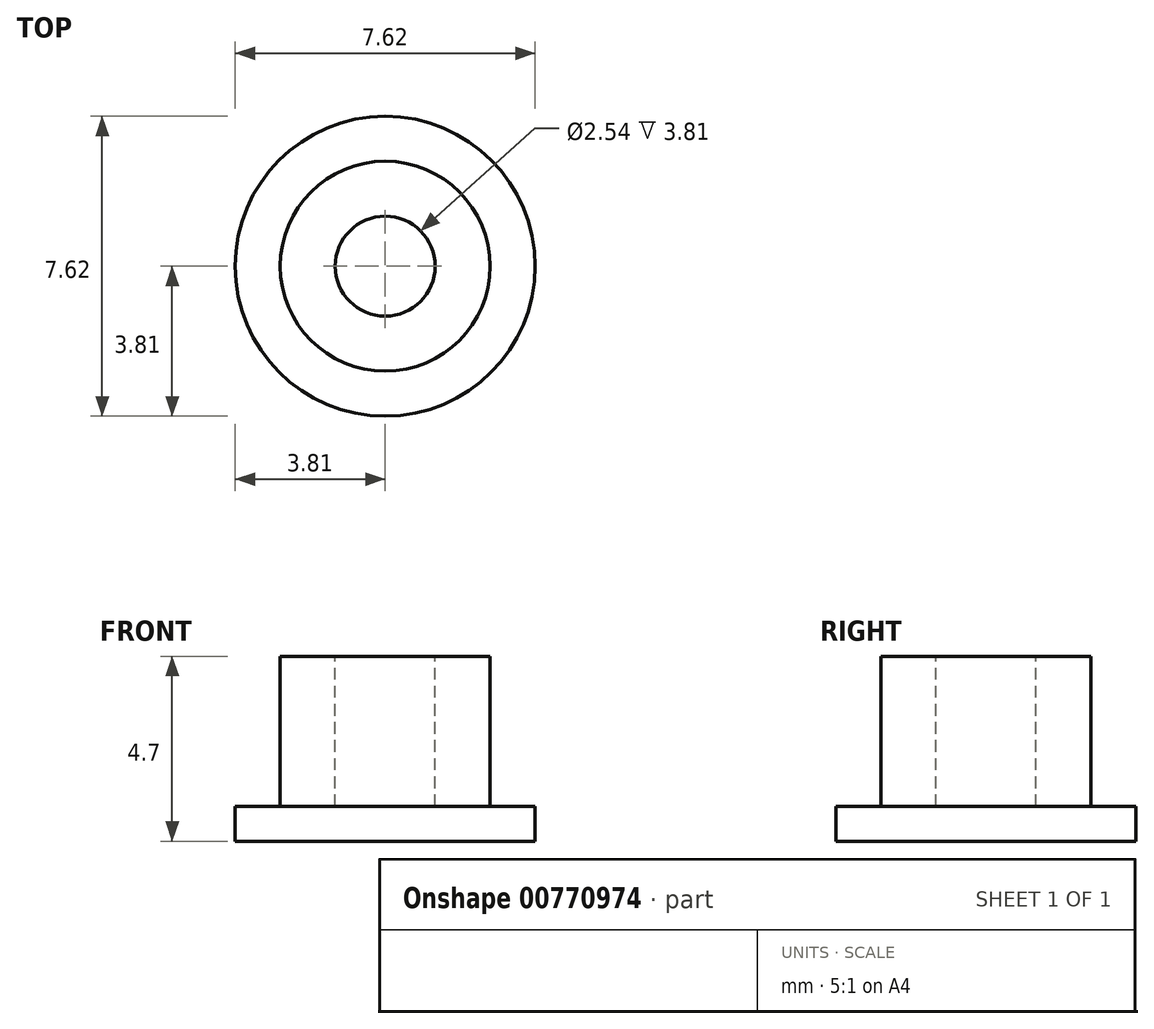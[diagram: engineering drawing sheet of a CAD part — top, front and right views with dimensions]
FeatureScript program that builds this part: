
annotation { "Feature Type Name" : "Feature", "Feature Type Description" : "" }
export const myFeature = defineFeature(function(context is Context, id is Id, definition is map)
    precondition{}
    {
        {
            var Q0;
            Q0=qCreatedBy(makeId("Top.planeOp"),FACE);
            var sketch = newSketch(context, id + "F0", { "sketchPlane" : qUnion([Q0])});
            skCircle(sketch, "E0", {"center": v(0, 0) * mm, "radius": 3.81 * mm});
            skSolve(sketch);
        }
        {
            var Q0;
            Q0=makeQuery(id+"F0.imprint","IMPRINT",FACE,{"disambiguationData":[TD([[makeQuery(id+"F0.imprint","IMPRINT",EDGE,{"derivedFrom":sQuery(id+"F0.wireOp",EDGE,"E0")}),1.0]])]});
            extrude(context, id + "F1", {"entities" : qUnion([Q0]), "depth" : 0.89 * mm, "offsetDistance" : 25.4 * mm});
        }
        {
            var Q0;
            Q0=makeQuery(id+"F1.opExtrude","CAP_FACE",FACE,{"disambiguationData":[OSD([sQuery(id+"F0.wireOp",EDGE,"E0")])],"isStart":false});
            var sketch = newSketch(context, id + "F2", { "sketchPlane" : qUnion([Q0])});
            skCircle(sketch, "E1", {"center": v(0, 0) * mm, "radius": 2.67 * mm});
            skSolve(sketch);
        }
        {
            var Q0;
            Q0=makeQuery(id+"F2.imprint","IMPRINT",FACE,{"disambiguationData":[TD([[makeQuery(id+"F2.imprint","IMPRINT",EDGE,{"derivedFrom":sQuery(id+"F2.wireOp",EDGE,"E1")}),1.0]])]});
            extrude(context, id + "F3", {"entities" : qUnion([Q0]), "operationType" : NewBodyOperationType.ADD, "depth" : 3.8 * mm, "offsetDistance" : 25.4 * mm});
        }
        {
            var Q0;
            Q0=makeQuery(id+"F3.opExtrude","CAP_FACE",FACE,{"disambiguationData":[OSD([sQuery(id+"F2.wireOp",EDGE,"E1")])],"isStart":false});
            var sketch = newSketch(context, id + "F4", { "sketchPlane" : qUnion([Q0])});
            skCircle(sketch, "E2", {"center": v(0, 0) * mm, "radius": 1.27 * mm});
            skSolve(sketch);
        }
        {
            var Q0;
            Q0=makeQuery(id+"F4.imprint","IMPRINT",FACE,{"disambiguationData":[TD([[makeQuery(id+"F4.imprint","IMPRINT",EDGE,{"derivedFrom":sQuery(id+"F4.wireOp",EDGE,"E2")}),1.0]])]});
            extrude(context, id + "F5", {"entities" : qUnion([Q0]), "operationType" : NewBodyOperationType.REMOVE, "oppositeDirection" : true, "depth" : 3.8 * mm, "offsetDistance" : 25.4 * mm});
        }
    });
